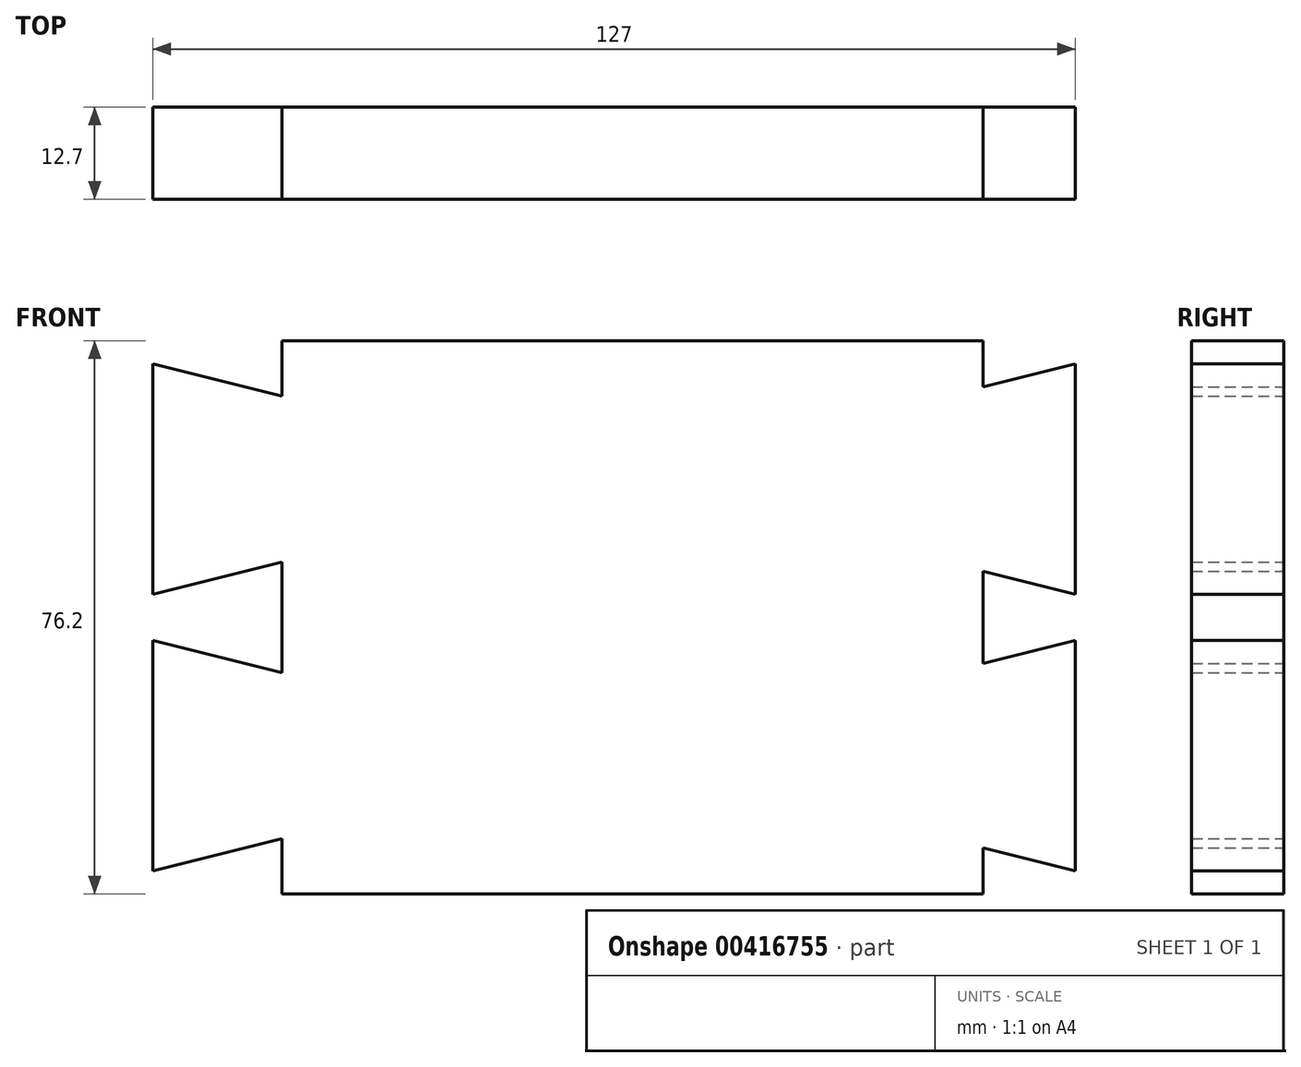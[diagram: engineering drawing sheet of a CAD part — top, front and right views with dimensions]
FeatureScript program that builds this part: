
annotation { "Feature Type Name" : "Feature", "Feature Type Description" : "" }
export const myFeature = defineFeature(function(context is Context, id is Id, definition is map)
    precondition{}
    {
        {
            var Q0;
            Q0=qCreatedBy(makeId("Front.planeOp"),FACE);
            var sketch = newSketch(context, id + "F0", { "sketchPlane" : qUnion([Q0])});
            skLineSegment(sketch, "E0.bottom", {"start": v(0, 0) * mm, "end": v(127, 0) * mm, "construction": true});
            skLineSegment(sketch, "E0.top", {"start": v(0, -38.1) * mm, "end": v(127, -38.1) * mm, "construction": true});
            skLineSegment(sketch, "E0.left", {"start": v(0, 0) * mm, "end": v(0, -38.1) * mm, "construction": true});
            skLineSegment(sketch, "E0.right", {"start": v(127, 0) * mm, "end": v(127, -38.1) * mm, "construction": true});
            skLineSegment(sketch, "E1", {"start": v(17.78, 0) * mm, "end": v(17.78, -38.1) * mm, "construction": true});
            skLineSegment(sketch, "E2", {"start": v(114.3, 0) * mm, "end": v(114.3, -38.1) * mm, "construction": true});
            skLineSegment(sketch, "E3", {"start": v(17.78, 0) * mm, "end": v(17.78, -7.6) * mm});
            skLineSegment(sketch, "E4", {"start": v(17.78, -7.6) * mm, "end": v(0, -3.17) * mm});
            skLineSegment(sketch, "E5", {"start": v(0, -3.18) * mm, "end": v(0, -34.93) * mm});
            skLineSegment(sketch, "E6", {"start": v(0, -34.93) * mm, "end": v(17.78, -30.5) * mm});
            skLineSegment(sketch, "E7", {"start": v(17.78, -30.5) * mm, "end": v(17.78, -38.1) * mm});
            skLineSegment(sketch, "E8", {"start": v(17.78, 0) * mm, "end": v(114.3, 0) * mm});
            skLineSegment(sketch, "E9", {"start": v(114.3, -6.34) * mm, "end": v(127, -3.18) * mm});
            skLineSegment(sketch, "E10", {"start": v(127, -3.18) * mm, "end": v(127, -34.93) * mm});
            skLineSegment(sketch, "E11", {"start": v(127, -34.92) * mm, "end": v(114.3, -31.76) * mm});
            skLineSegment(sketch, "E12", {"start": v(114.3, -31.76) * mm, "end": v(114.3, -38.1) * mm});
            skLineSegment(sketch, "E13.MirrorCS", {"start": v(17.78, -45.7) * mm, "end": v(17.78, -38.1) * mm});
            skLineSegment(sketch, "E14.MirrorCS", {"start": v(0, -41.27) * mm, "end": v(17.78, -45.7) * mm});
            skLineSegment(sketch, "E15.MirrorCS", {"start": v(0, -73.03) * mm, "end": v(0, -41.27) * mm});
            skLineSegment(sketch, "E16.MirrorCS", {"start": v(17.78, -68.6) * mm, "end": v(0, -73.03) * mm});
            skLineSegment(sketch, "E17.MirrorCS", {"start": v(17.78, -76.2) * mm, "end": v(17.78, -68.6) * mm});
            skLineSegment(sketch, "E18.MirrorCS", {"start": v(17.78, -76.2) * mm, "end": v(114.3, -76.2) * mm});
            skLineSegment(sketch, "E19.MirrorCS", {"start": v(114.3, -76.2) * mm, "end": v(114.3, -38.1) * mm, "construction": true});
            skLineSegment(sketch, "E20", {"start": v(114.3, 0) * mm, "end": v(114.3, -6.34) * mm});
            skLineSegment(sketch, "E21.MirrorCS", {"start": v(114.3, -76.2) * mm, "end": v(114.3, -69.86) * mm});
            skLineSegment(sketch, "E22.MirrorCS", {"start": v(114.3, -69.86) * mm, "end": v(127, -73.03) * mm});
            skLineSegment(sketch, "E23.MirrorCS", {"start": v(127, -73.03) * mm, "end": v(127, -41.27) * mm});
            skLineSegment(sketch, "E24.MirrorCS", {"start": v(127, -41.28) * mm, "end": v(114.3, -44.44) * mm});
            skLineSegment(sketch, "E25.MirrorCS", {"start": v(114.3, -44.44) * mm, "end": v(114.3, -38.1) * mm});
            skSolve(sketch);
        }
        {
            var Q0;
            Q0=makeQuery(id+"F0.imprint","IMPRINT",FACE,{"disambiguationData":[TD([[makeQuery(id+"F0.imprint","IMPRINT",EDGE,{"derivedFrom":sQuery(id+"F0.wireOp",EDGE,"E3")}),1.0]])]});
            extrude(context, id + "F1", {"entities" : qUnion([Q0]), "depth" : 12.7 * mm});
        }
    });
